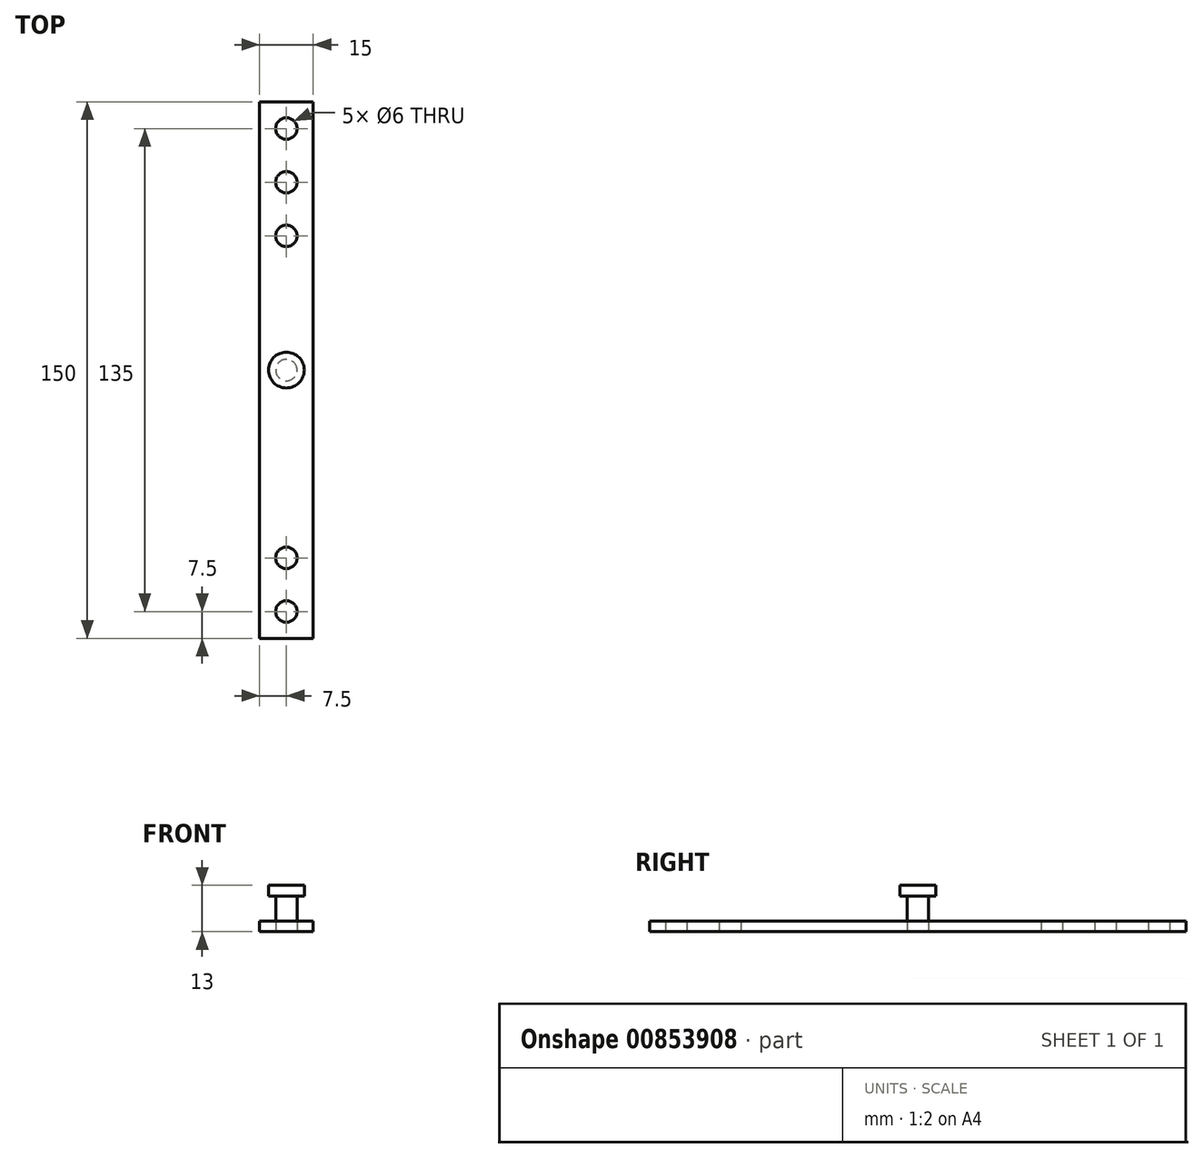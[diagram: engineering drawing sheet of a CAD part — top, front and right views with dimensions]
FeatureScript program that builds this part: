
annotation { "Feature Type Name" : "Feature", "Feature Type Description" : "" }
export const myFeature = defineFeature(function(context is Context, id is Id, definition is map)
    precondition{}
    {
        {
            var Q0;
            Q0=qCreatedBy(makeId("Top.planeOp"),FACE);
            var sketch = newSketch(context, id + "F0", { "sketchPlane" : qUnion([Q0])});
            skLineSegment(sketch, "E0.bottom", {"start": v(7.5, 75) * mm, "end": v(-7.5, 75) * mm});
            skLineSegment(sketch, "E0.top", {"start": v(7.5, -75) * mm, "end": v(-7.5, -75) * mm});
            skLineSegment(sketch, "E0.left", {"start": v(7.5, 75) * mm, "end": v(7.5, -75) * mm});
            skLineSegment(sketch, "E0.right", {"start": v(-7.5, 75) * mm, "end": v(-7.5, -75) * mm});
            skPoint(sketch, "E0.middle", {"position": v(0, 0) * mm});
            skCircle(sketch, "E1", {"center": v(0, 67.5) * mm, "radius": 3 * mm});
            skCircle(sketch, "E2", {"center": v(0, -67.5) * mm, "radius": 3 * mm});
            skCircle(sketch, "E3", {"center": v(0, 52.5) * mm, "radius": 3 * mm});
            skCircle(sketch, "E4", {"center": v(0, -52.5) * mm, "radius": 3 * mm});
            skCircle(sketch, "E5", {"center": v(0, 37.5) * mm, "radius": 3 * mm});
            skSolve(sketch);
        }
        {
            var Q0;
            Q0 = qSketchRegion(id + "F0", true);
            extrude(context, id + "F1", {"entities" : qUnion([Q0]), "depth" : 3 * mm, "offsetDistance" : 25 * mm});
        }
        {
            var Q0;
            Q0=qCreatedBy(makeId("Top.planeOp"),FACE);
            var sketch = newSketch(context, id + "F2", { "sketchPlane" : qUnion([Q0])});
            skCircle(sketch, "E6", {"center": v(0, 0) * mm, "radius": 3 * mm});
            skSolve(sketch);
        }
        {
            var Q0;
            Q0 = qSketchRegion(id + "F2", true);
            extrude(context, id + "F3", {"entities" : qUnion([Q0]), "depth" : 10 * mm, "offsetDistance" : 25 * mm});
        }
        {
            var Q0;
            Q0=makeQuery(id+"F3.opExtrude","CAP_FACE",FACE,{"disambiguationData":[OSD([sQuery(id+"F2.wireOp",EDGE,"E6")])],"isStart":false});
            var sketch = newSketch(context, id + "F4", { "sketchPlane" : qUnion([Q0])});
            skCircle(sketch, "E7", {"center": v(0, 0) * mm, "radius": 5 * mm});
            skSolve(sketch);
        }
        {
            var Q0;
            Q0 = qSketchRegion(id + "F4", true);
            extrude(context, id + "F5", {"entities" : qUnion([Q0]), "operationType" : NewBodyOperationType.ADD, "depth" : 3 * mm, "offsetDistance" : 25 * mm});
        }
    });
